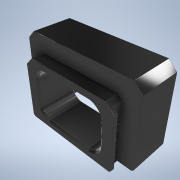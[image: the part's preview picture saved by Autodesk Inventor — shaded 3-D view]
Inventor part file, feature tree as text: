
AUTODESK INVENTOR PART (.ipt)
format: ipt  version: 2020.2 (Build 242310000, 310)  size: 754,176 bytes
history: native  units: mm
features: fillet x9, extrude x7, sketch x7, projected_geometry x3, chamfer x2, mirror x1
ambient origin geometry x8: Origin, YZ Plane, XZ Plane, XY Plane, X Axis, Y Axis, Z Axis, Center Point
bodies: Solid1 (feature_tree)
feature tree (29):
  extrude  "Extrusion1"  Depth=20.0mm
  extrude  "Extrusion2"  Depth=12.0mm
  extrude  "Extrusion3"  Depth=22.0mm
  extrude  "Extrusion4"  Depth=2.2mm TaperAngle=0.0deg
  extrude  "Extrusion5"  Depth=1.0mm TaperAngle=0.0deg
  extrude  "Extrusion6"  Depth=0.6mm TaperAngle=0.0deg
  fillet  "Fillet3"  Radius=6.8mm
  fillet  "Fillet1"  Radius=1.5mm
  mirror  "Mirror1"
  chamfer  "Chamfer1"  Distance=16.0mm
  chamfer  "Chamfer2"  Distance=3.0mm
  extrude  "Extrusion7"  Depth=22.6mm
  fillet  "Fillet4"  Radius=11.3mm
  fillet  "Fillet5"  Radius=21.6mm
  fillet  "Fillet6"  Radius=10.8mm
  fillet  "Fillet7"  [1 undecoded]
  fillet  "Fillet8"  [1 undecoded]
  fillet  "Fillet9"  [1 undecoded]
  fillet  "Fillet10"  [1 undecoded]
  sketch  "Sketch1"  dims[d0=30.0mm d1=20.0mm]
  sketch  "Sketch2"  dims[d2=18.0mm d3=12.0mm]
  projected_geometry  "Projected Loop1"
  sketch  "Sketch3"  dims[d4=7.0mm d5=0.0mm d6=22.0mm]
  sketch  "Sketch4"  dims[d7=16.0mm d8=2.2mm d9=0.0mm]
  projected_geometry  "Projected Loop2"
  sketch  "Sketch5"  dims[d10=24.2mm d11=1.0mm d12=0.0mm]
  projected_geometry  "Projected Loop3"
  sketch  "Sketch6"  dims[d13=2.0mm d17=0.6mm d18=0.0mm d19=6.8mm d20=1.5mm]
  sketch  "Sketch8"  dims[d21=25.0mm d22=16.0mm d23=3.0mm d24=0.0mm d26=22.6mm d27=11.3mm d28=21.6mm d29=10.8mm d30=45.0deg d31=45.0deg d32=45.0deg d33=45.0deg d34=7.5mm d35=2.0mm d36=1.4mm d37=0.0mm d38=3.0mm d40=2.0mm d41=2.0mm d42=2.0mm d43=45.0deg d44=0.5mm d45=2.0mm d46=45.0deg d47=10.0mm d48=0.0mm d49=0.1mm d50=0.1mm d51=0.1mm d52=0.1mm d53=0.1mm d54=0.1mm d55=0.1mm]
note: 4 required parameter values undecoded (feature->parameter linkage not recoverable at this tier; creation-order binding heuristic only, values carry confidence <= 0.55)
